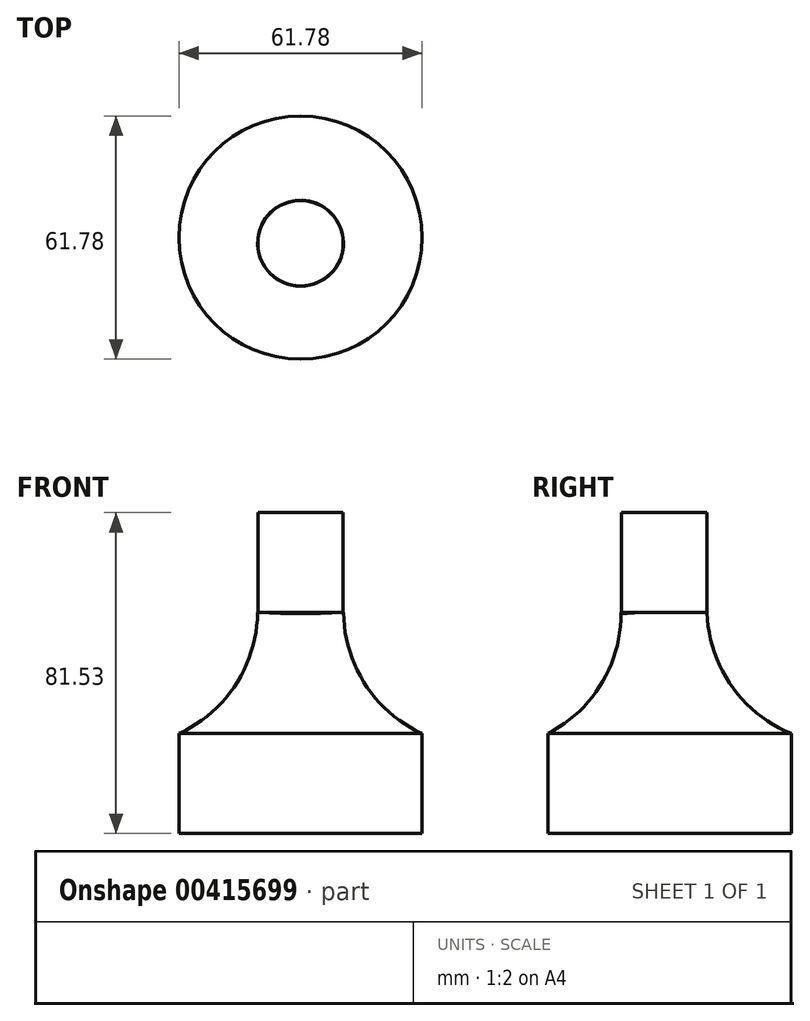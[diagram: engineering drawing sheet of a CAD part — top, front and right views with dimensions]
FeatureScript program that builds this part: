
annotation { "Feature Type Name" : "Feature", "Feature Type Description" : "" }
export const myFeature = defineFeature(function(context is Context, id is Id, definition is map)
    precondition{}
    {
        {
            var Q0;
            Q0=qCreatedBy(makeId("Top.planeOp"),FACE);
            var sketch = newSketch(context, id + "F0", { "sketchPlane" : qUnion([Q0])});
            skCircle(sketch, "E0", {"center": v(0, 1.44) * mm, "radius": 30.9 * mm});
            skSolve(sketch);
        }
        {
            var Q0;
            Q0 = qSketchRegion(id + "F0", true);
            extrude(context, id + "F1", {"entities" : qUnion([Q0]), "depth" : 25.4 * mm});
        }
        {
            var Q0;
            Q0=qCreatedBy(makeId("Top.planeOp"),FACE);
            var sketch = newSketch(context, id + "F2", { "sketchPlane" : qUnion([Q0])});
            skCircle(sketch, "E1", {"center": v(0, 0) * mm, "radius": 10.92 * mm});
            skSolve(sketch);
        }
        {
            var Q0;
            Q0=makeQuery(id+"F2.imprint","IMPRINT",FACE,{"disambiguationData":[TD([[makeQuery(id+"F2.imprint","IMPRINT",EDGE,{"derivedFrom":sQuery(id+"F2.wireOp",EDGE,"E1")}),1.0]])]});
            extrude(context, id + "F3", {"entities" : qUnion([Q0]), "operationType" : NewBodyOperationType.ADD, "depth" : 56.13 * mm});
        }
        {
            var Q0;
            Q0=makeQuery(id+"F3.boolean.opBoolean","INTERSECT",EDGE,{"derivedFrom":[makeQuery(id+"F1.opExtrude","CAP_FACE",FACE,{"disambiguationData":[OSD([sQuery(id+"F0.wireOp",EDGE,"E0")])],"isStart":false}),makeQuery(id+"F3.opExtrude","SWEPT_FACE",FACE,{"disambiguationData":[OSD([sQuery(id+"F2.wireOp",EDGE,"E1")])]})]});
            fillet(context, id + "F4", {"entities" : qUnion([Q0]), "radius" : 34.34 * mm, "tangentPropagation" : true, "allowEdgeOverflow" : false});
        }
        {
            var Q0;
            Q0=makeQuery(id+"F3.opExtrude","CAP_FACE",FACE,{"disambiguationData":[OSD([sQuery(id+"F2.wireOp",EDGE,"E1")])],"isStart":false});
            var sketch = newSketch(context, id + "F5", { "sketchPlane" : qUnion([Q0])});
            skCircle(sketch, "E2", {"center": v(0, 0) * mm, "radius": 10.85 * mm});
            skSolve(sketch);
        }
        {
            var Q0;
            Q0 = qSketchRegion(id + "F5", true);
            extrude(context, id + "F6", {"entities" : qUnion([Q0]), "operationType" : NewBodyOperationType.ADD, "depth" : 25.4 * mm});
        }
    });
